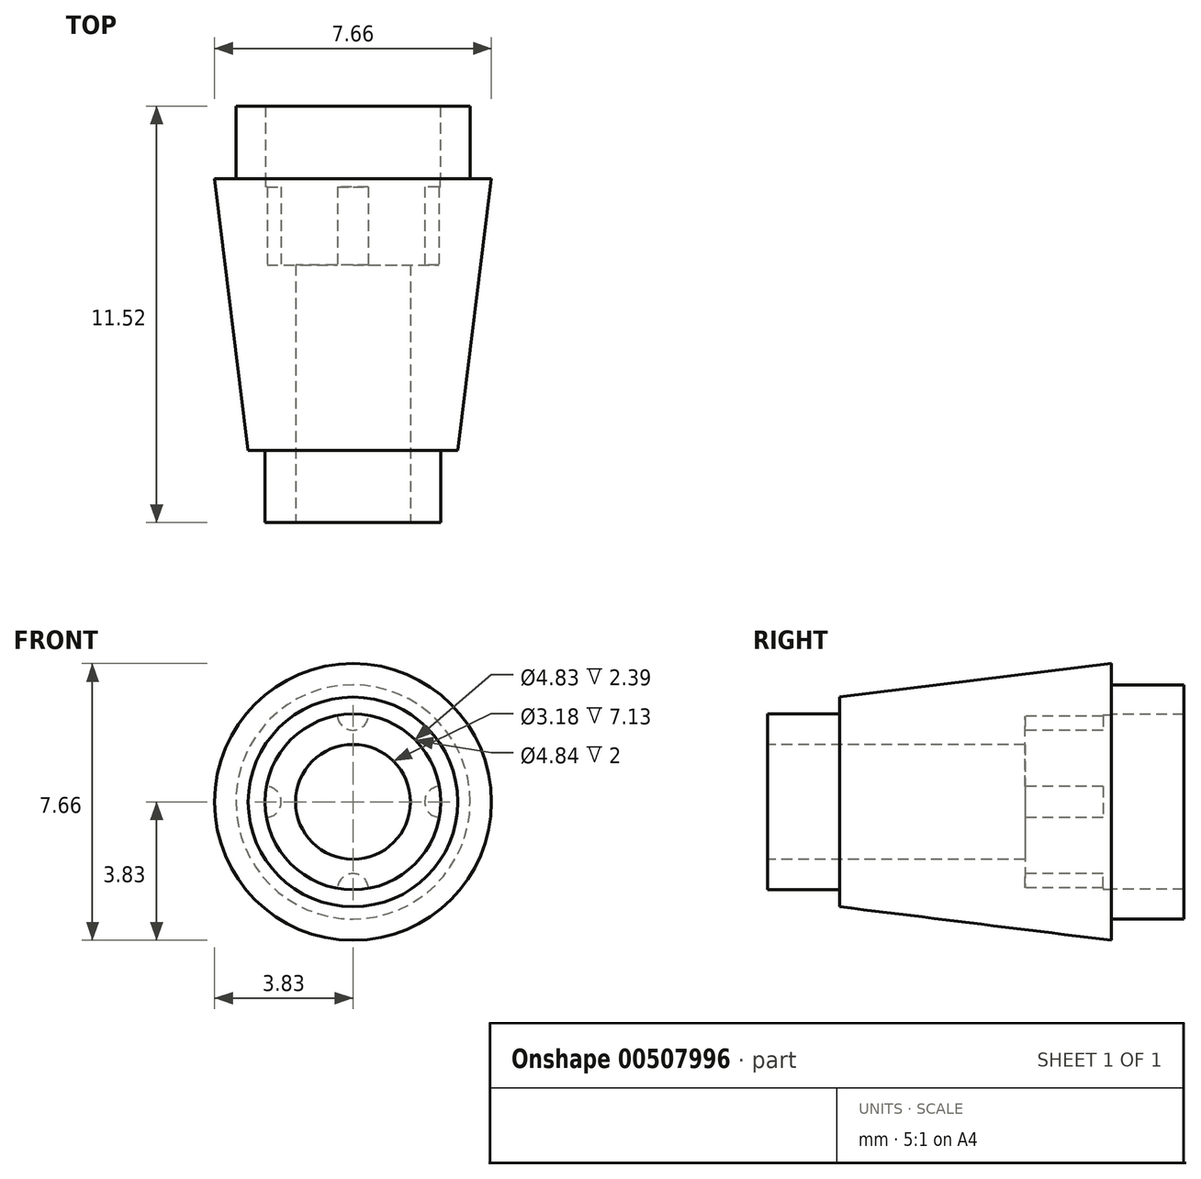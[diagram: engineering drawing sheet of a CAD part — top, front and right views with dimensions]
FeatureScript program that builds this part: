
annotation { "Feature Type Name" : "Feature", "Feature Type Description" : "" }
export const myFeature = defineFeature(function(context is Context, id is Id, definition is map)
    precondition{}
    {
        {
            var Q0;
            Q0=qCreatedBy(makeId("Front.planeOp"),FACE);
            var sketch = newSketch(context, id + "F0", { "sketchPlane" : qUnion([Q0])});
            skCircle(sketch, "E0", {"center": v(0, 0) * mm, "radius": 3.83 * mm});
            skSolve(sketch);
        }
        {
            var Q0;
            Q0 = qSketchRegion(id + "F0", true);
            extrude(context, id + "F1", {"entities" : qUnion([Q0]), "depth" : 7.52 * mm, "offsetDistance" : 25 * mm});
        }
        {
            var Q0;
            Q0=makeQuery(id+"F1.opExtrude","CAP_FACE",FACE,{"disambiguationData":[OSD([sQuery(id+"F0.wireOp",EDGE,"E0")])],"isStart":false});
            var sketch = newSketch(context, id + "F2", { "sketchPlane" : qUnion([Q0])});
            skCircle(sketch, "E1", {"center": v(0, 0) * mm, "radius": 2.9 * mm});
            skSolve(sketch);
        }
        {
            var Q1;
            Q1=makeQuery(id+"F1.opExtrude","CAP_FACE",FACE,{"disambiguationData":[OSD([sQuery(id+"F0.wireOp",EDGE,"E0")])],"isStart":true});
            var Q2;
            Q2=makeQuery(id+"F2.imprint","IMPRINT",FACE,{"disambiguationData":[TD([[makeQuery(id+"F2.imprint","IMPRINT",EDGE,{"derivedFrom":sQuery(id+"F2.wireOp",EDGE,"E1")}),1.0]])]});
            loft(context, id + "F3", {"operationType" : NewBodyOperationType.INTERSECT, "sheetProfilesArray" : [{ "sheetProfileEntities" : qUnion([Q1]) }, { "sheetProfileEntities" : qUnion([Q2]) }]});
        }
        {
            var Q0;
            Q0=makeQuery(id+"F1.opExtrude","CAP_FACE",FACE,{"disambiguationData":[OSD([sQuery(id+"F0.wireOp",EDGE,"E0")])],"isStart":false});
            var sketch = newSketch(context, id + "F4", { "sketchPlane" : qUnion([Q0])});
            skCircle(sketch, "E2", {"center": v(0, 0) * mm, "radius": 2.43 * mm});
            skSolve(sketch);
        }
        {
            var Q0;
            Q0 = qSketchRegion(id + "F4", true);
            extrude(context, id + "F5", {"entities" : qUnion([Q0]), "operationType" : NewBodyOperationType.ADD, "depth" : 2 * mm, "offsetDistance" : 25 * mm});
        }
        {
            var Q0;
            Q0=makeQuery(id+"F5.opExtrude","CAP_FACE",FACE,{"disambiguationData":[OSD([sQuery(id+"F4.wireOp",EDGE,"E2")])],"isStart":false});
            var sketch = newSketch(context, id + "F6", { "sketchPlane" : qUnion([Q0])});
            skCircle(sketch, "E3", {"center": v(0, 0) * mm, "radius": 1.59 * mm});
            skSolve(sketch);
        }
        {
            var Q0;
            Q0 = qSketchRegion(id + "F6", true);
            extrude(context, id + "F7", {"entities" : qUnion([Q0]), "operationType" : NewBodyOperationType.REMOVE, "endBound" : BoundingType.THROUGH_ALL, "oppositeDirection" : true, "depth" : 25 * mm, "offsetDistance" : 25 * mm});
        }
        {
            var Q0;
            Q0=makeQuery(id+"F1.opExtrude","CAP_FACE",FACE,{"disambiguationData":[OSD([sQuery(id+"F0.wireOp",EDGE,"E0")])],"isStart":true});
            var sketch = newSketch(context, id + "F8", { "sketchPlane" : qUnion([Q0])});
            skCircle(sketch, "E4", {"center": v(0, 0) * mm, "radius": 3.24 * mm});
            skCircle(sketch, "E5", {"center": v(0, 0) * mm, "radius": 2.42 * mm});
            skSolve(sketch);
        }
        {
            var Q0;
            Q0 = qSketchRegion(id + "F8", true);
            extrude(context, id + "F9", {"entities" : qUnion([Q0]), "operationType" : NewBodyOperationType.ADD, "depth" : 2 * mm, "offsetDistance" : 25 * mm});
        }
        {
            var Q0;
            Q0=makeQuery(id+"F9.opExtrude","CAP_FACE",FACE,{"disambiguationData":[OSD([sQuery(id+"F8.wireOp",EDGE,"E4"),sQuery(id+"F8.wireOp",EDGE,"E5")])],"isStart":false});
            var sketch = newSketch(context, id + "F10", { "sketchPlane" : qUnion([Q0])});
            skCircle(sketch, "E6", {"center": v(0, 0) * mm, "radius": 2.41 * mm});
            skSolve(sketch);
        }
        {
            var Q0;
            Q0 = qSketchRegion(id + "F10", true);
            extrude(context, id + "F11", {"entities" : qUnion([Q0]), "operationType" : NewBodyOperationType.REMOVE, "oppositeDirection" : true, "depth" : 4.39 * mm, "offsetDistance" : 25 * mm});
        }
        {
            var Q0;
            Q0=makeQuery(id+"F11.boolean.opBoolean","COPY",FACE,{"derivedFrom":makeQuery(id+"F11.opExtrude","CAP_FACE",FACE,{"disambiguationData":[OSD([sQuery(id+"F10.wireOp",EDGE,"E6")])],"isStart":false})});
            var sketch = newSketch(context, id + "F12", { "sketchPlane" : qUnion([Q0])});
            skCircle(sketch, "E7", {"center": v(0, 2.41) * mm, "radius": 0.43 * mm});
            skCircle(sketch, "E8.1.0", {"center": v(-2.41, 0) * mm, "radius": 0.43 * mm});
            skCircle(sketch, "E8.2.0", {"center": v(0, -2.41) * mm, "radius": 0.43 * mm});
            skCircle(sketch, "E8.3.0", {"center": v(2.41, 0) * mm, "radius": 0.43 * mm});
            skPoint(sketch, "E8.center", {"position": v(0, 0) * mm});
            skSolve(sketch);
        }
        {
            var Q0;
            Q0 = qSketchRegion(id + "F12", true);
            extrude(context, id + "F13", {"entities" : qUnion([Q0]), "operationType" : NewBodyOperationType.ADD, "depth" : 2.16 * mm, "offsetDistance" : 25 * mm});
        }
    });
